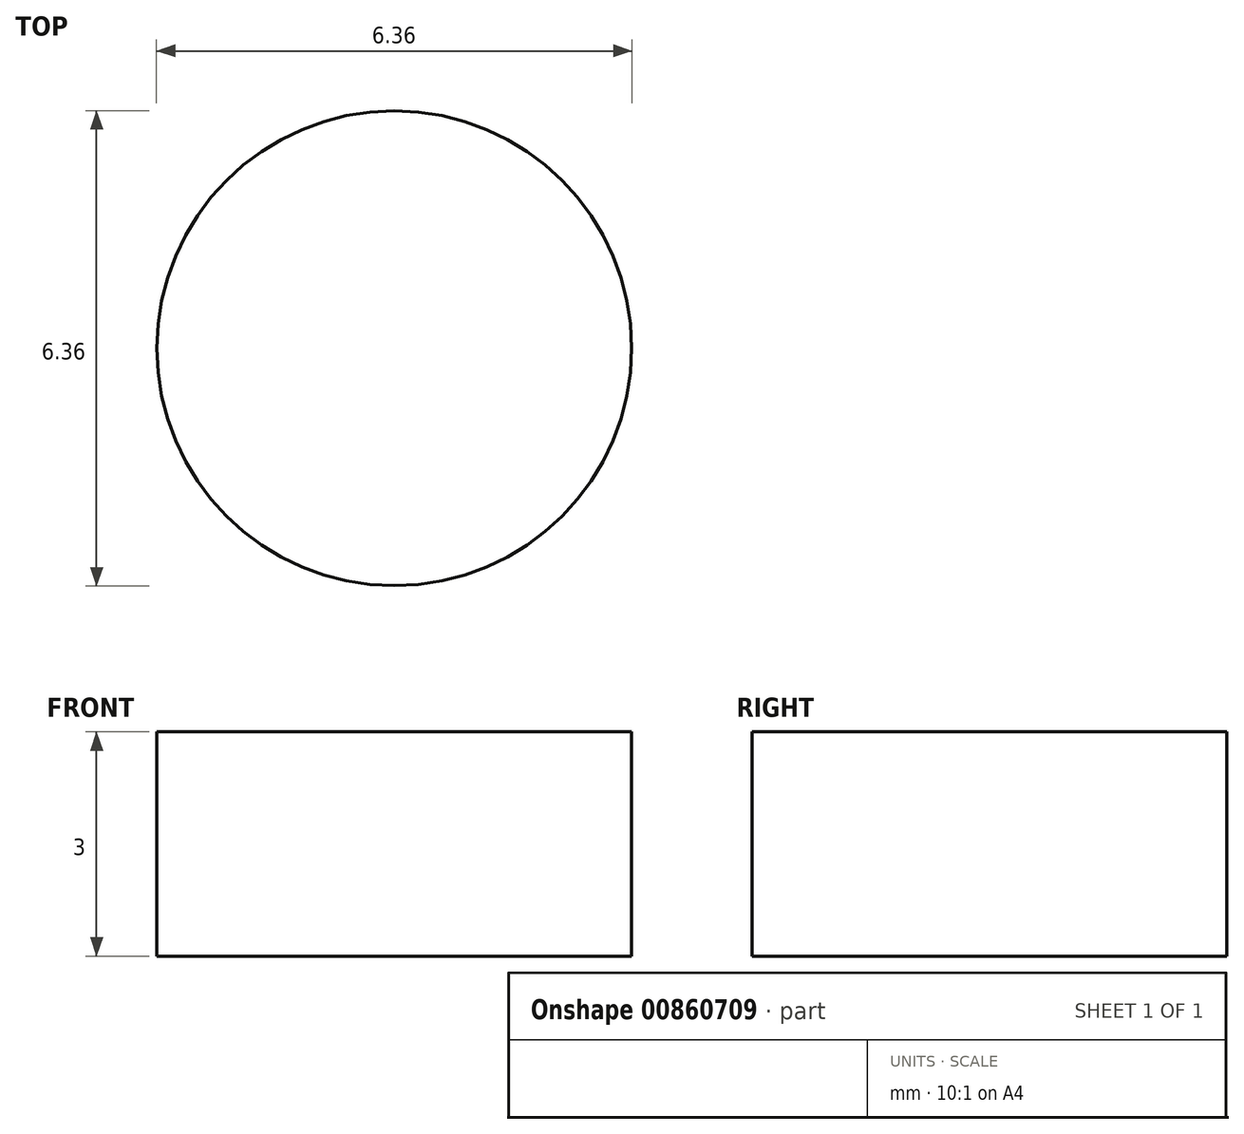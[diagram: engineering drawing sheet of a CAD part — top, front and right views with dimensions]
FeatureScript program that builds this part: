
annotation { "Feature Type Name" : "Feature", "Feature Type Description" : "" }
export const myFeature = defineFeature(function(context is Context, id is Id, definition is map)
    precondition{}
    {
        {
            assignVariable(context, id + "F0", {"name" : "DowelLen", "anyValue" : 3});
        }
        {
            var Q0;
            Q0=qCreatedBy(makeId("Top.planeOp"),FACE);
            var sketch = newSketch(context, id + "F1", { "sketchPlane" : qUnion([Q0])});
            skCircle(sketch, "E0", {"center": v(0, 0) * mm, "radius": 3.18 * mm});
            skSolve(sketch);
        }
        {
            var Q0;
            Q0 = qSketchRegion(id + "F1", true);
            extrude(context, id + "F2", {"entities" : qUnion([Q0]), "depth" : (getVariable(context, 'DowelLen')) * mm, "offsetDistance" : 25.4 * mm});
        }
    });
